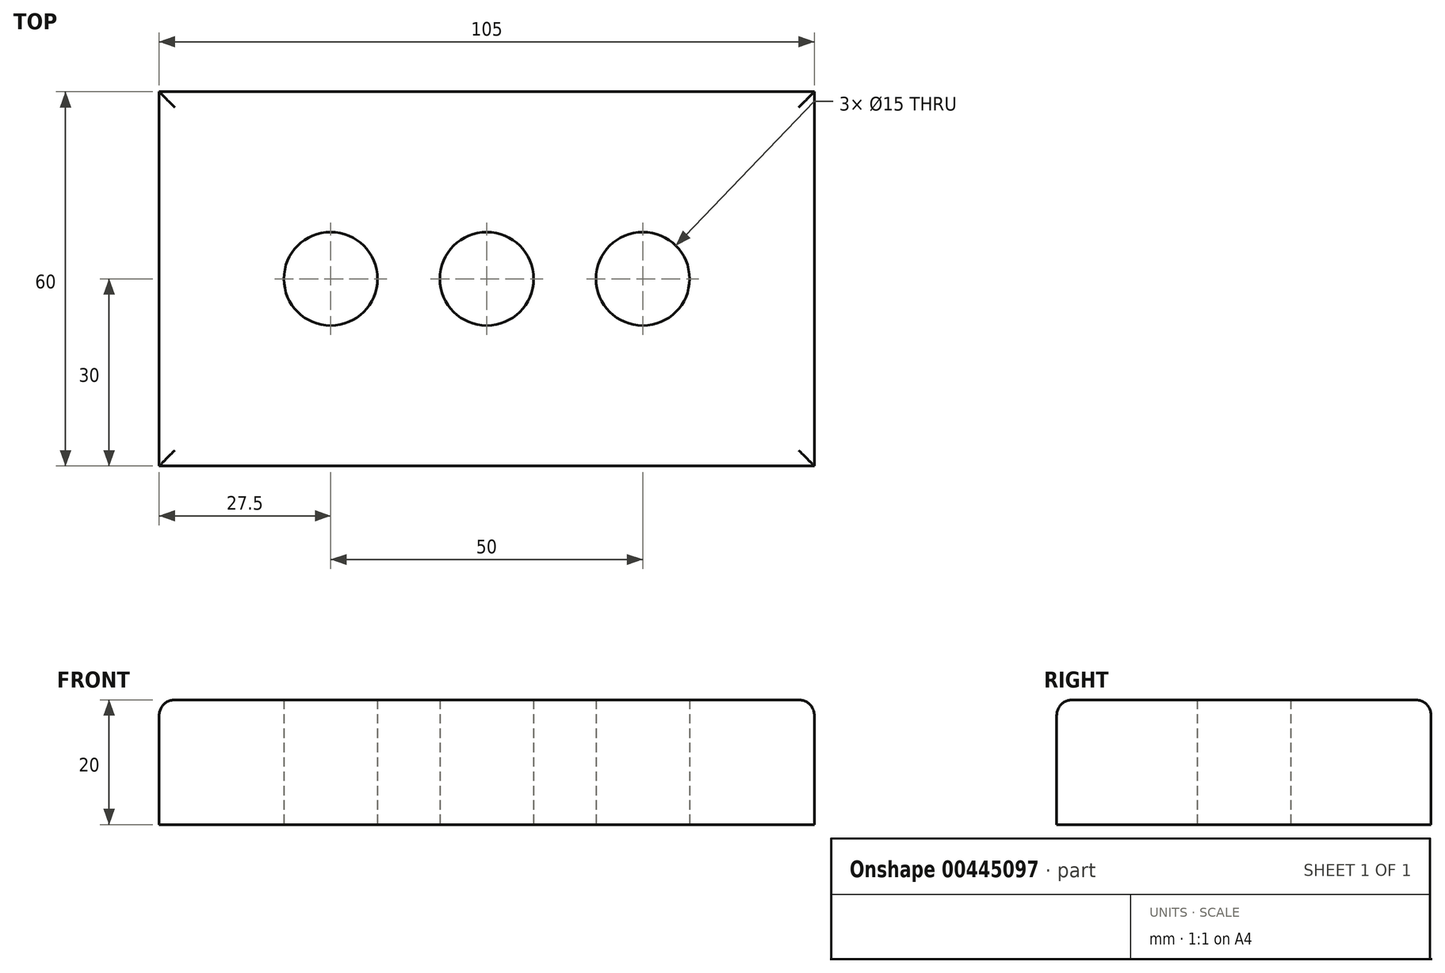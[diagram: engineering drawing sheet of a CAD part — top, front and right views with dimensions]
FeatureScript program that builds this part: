
annotation { "Feature Type Name" : "Feature", "Feature Type Description" : "" }
export const myFeature = defineFeature(function(context is Context, id is Id, definition is map)
    precondition{}
    {
        {
            var Q0;
            Q0=qCreatedBy(makeId("Top.planeOp"),FACE);
            var sketch = newSketch(context, id + "F0", { "sketchPlane" : qUnion([Q0])});
            skLineSegment(sketch, "E0.bottom", {"start": v(52.5, 30) * mm, "end": v(-52.5, 30) * mm});
            skLineSegment(sketch, "E0.top", {"start": v(52.5, -30) * mm, "end": v(-52.5, -30) * mm});
            skLineSegment(sketch, "E0.left", {"start": v(52.5, 30) * mm, "end": v(52.5, -30) * mm});
            skLineSegment(sketch, "E0.right", {"start": v(-52.5, 30) * mm, "end": v(-52.5, -30) * mm});
            skPoint(sketch, "E0.middle", {"position": v(0, 0) * mm});
            skCircle(sketch, "E1", {"center": v(0, 0) * mm, "radius": 7.5 * mm});
            skCircle(sketch, "E2", {"center": v(-25, 0) * mm, "radius": 7.5 * mm});
            skCircle(sketch, "E3", {"center": v(25, 0) * mm, "radius": 7.5 * mm});
            skSolve(sketch);
        }
        {
            var Q0;
            Q0 = qSketchRegion(id + "F0", true);
            extrude(context, id + "F1", {"entities" : qUnion([Q0]), "depth" : 20 * mm});
        }
        {
            var Q0;
            Q0=makeQuery(id+"F1.opExtrude","CAP_EDGE",EDGE,{"disambiguationData":[OSD([sQuery(id+"F0.wireOp",EDGE,"E0.bottom")])],"isStart":false});
            var Q1;
            Q1=makeQuery(id+"F1.opExtrude","CAP_EDGE",EDGE,{"disambiguationData":[OSD([sQuery(id+"F0.wireOp",EDGE,"E0.right")])],"isStart":false});
            var Q2;
            Q2=makeQuery(id+"F1.opExtrude","CAP_EDGE",EDGE,{"disambiguationData":[OSD([sQuery(id+"F0.wireOp",EDGE,"E0.top")])],"isStart":false});
            var Q3;
            Q3=makeQuery(id+"F1.opExtrude","CAP_EDGE",EDGE,{"disambiguationData":[OSD([sQuery(id+"F0.wireOp",EDGE,"E0.left")])],"isStart":false});
            fillet(context, id + "F2", {"entities" : qUnion([Q0, Q1, Q2, Q3]), "radius" : 2.5 * mm, "tangentPropagation" : true, "allowEdgeOverflow" : false});
        }
    });
